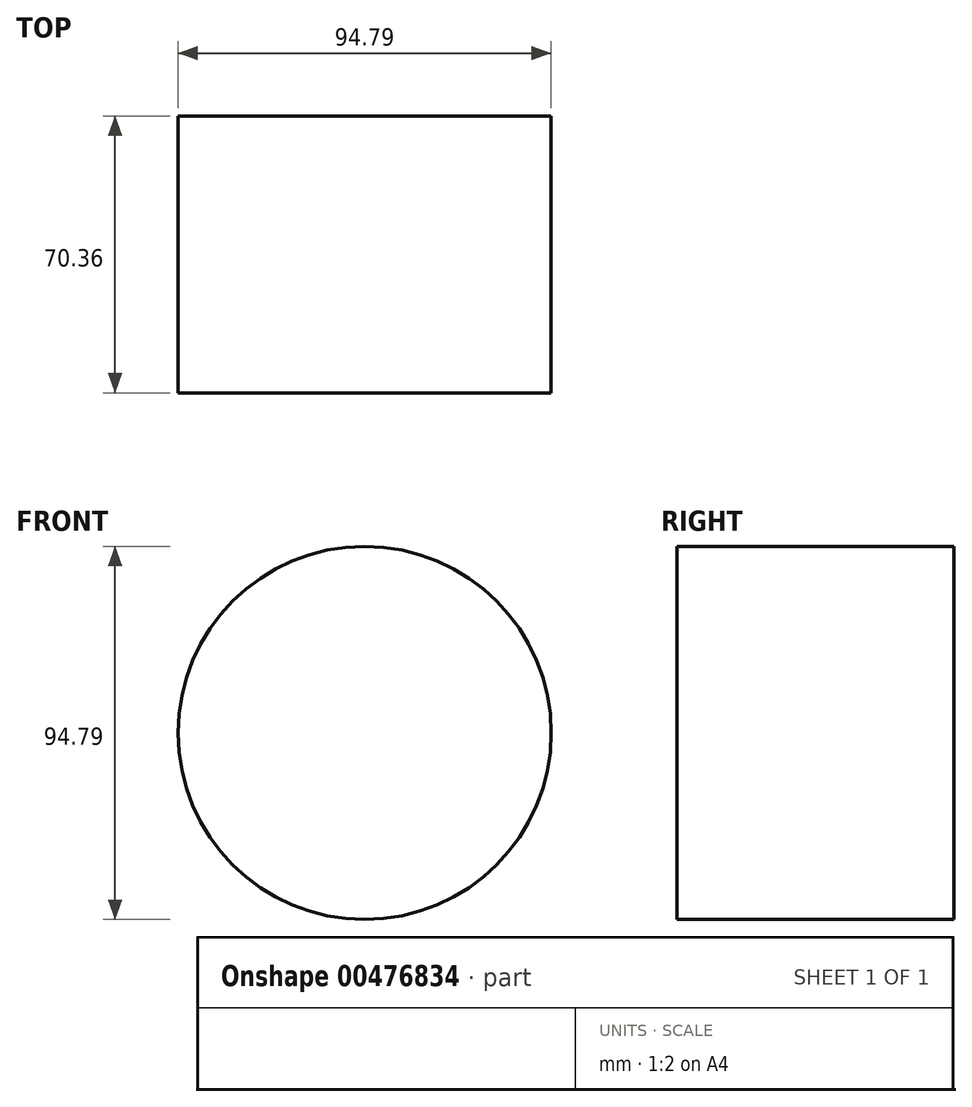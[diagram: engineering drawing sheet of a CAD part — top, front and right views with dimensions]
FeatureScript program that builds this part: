
annotation { "Feature Type Name" : "Feature", "Feature Type Description" : "" }
export const myFeature = defineFeature(function(context is Context, id is Id, definition is map)
    precondition{}
    {
        {
            var Q0;
            Q0=qCreatedBy(makeId("Front.planeOp"),FACE);
            var sketch = newSketch(context, id + "F0", { "sketchPlane" : qUnion([Q0])});
            skCircle(sketch, "E0", {"center": v(-10.12, -4.32) * mm, "radius": 47.4 * mm});
            skCircle(sketch, "E1", {"center": v(-10.12, -4.32) * mm, "radius": 25.6 * mm});
            skSolve(sketch);
        }
        {
            var Q0;
            Q0=makeQuery(id+"F0.imprint","IMPRINT",FACE,{"disambiguationData":[TD([[makeQuery(id+"F0.imprint","IMPRINT",EDGE,{"derivedFrom":sQuery(id+"F0.wireOp",EDGE,"E1")}),1.0]])]});
            var Q1;
            Q1=makeQuery(id+"F0.imprint","IMPRINT",FACE,{"disambiguationData":[TD([[makeQuery(id+"F0.imprint","IMPRINT",EDGE,{"derivedFrom":sQuery(id+"F0.wireOp",EDGE,"E0")}),1.0]])]});
            extrude(context, id + "F1", {"entities" : qUnion([Q0, Q1]), "depth" : 70.36 * mm});
        }
    });
